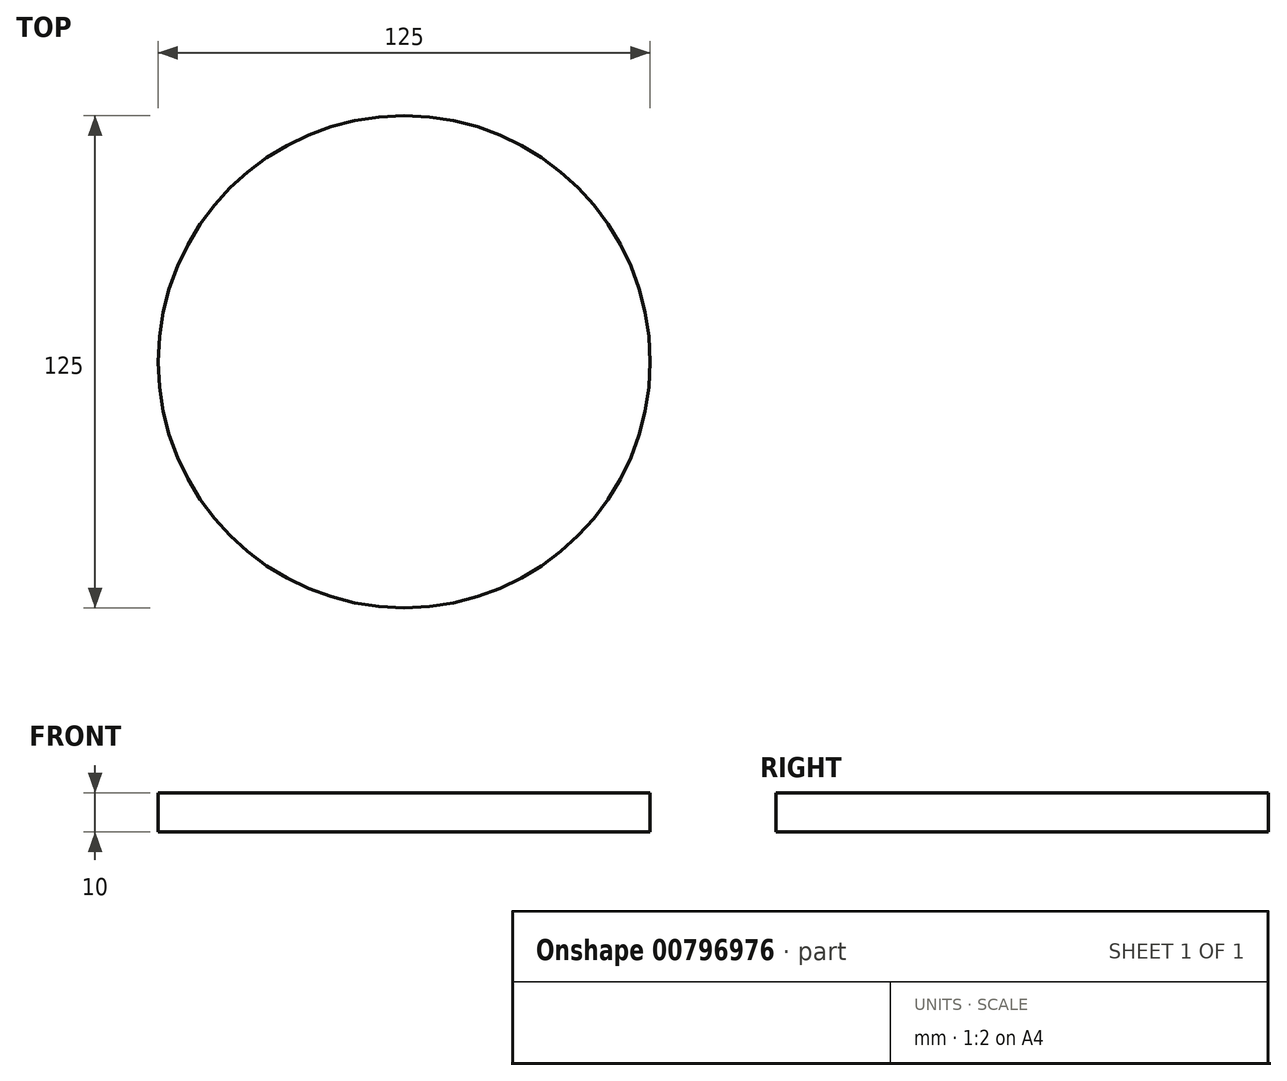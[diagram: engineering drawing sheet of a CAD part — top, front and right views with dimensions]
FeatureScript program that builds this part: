
annotation { "Feature Type Name" : "Feature", "Feature Type Description" : "" }
export const myFeature = defineFeature(function(context is Context, id is Id, definition is map)
    precondition{}
    {
        {
            var Q0;
            Q0=qCreatedBy(makeId("Top.planeOp"),FACE);
            var sketch = newSketch(context, id + "F0", { "sketchPlane" : qUnion([Q0])});
            skCircle(sketch, "E0", {"center": v(0, 0) * mm, "radius": 62.5 * mm});
            skSolve(sketch);
        }
        {
            var Q0;
            Q0 = qSketchRegion(id + "F0", true);
            extrude(context, id + "F1", {"entities" : qUnion([Q0]), "depth" : 10 * mm, "offsetDistance" : 25 * mm});
        }
    });
